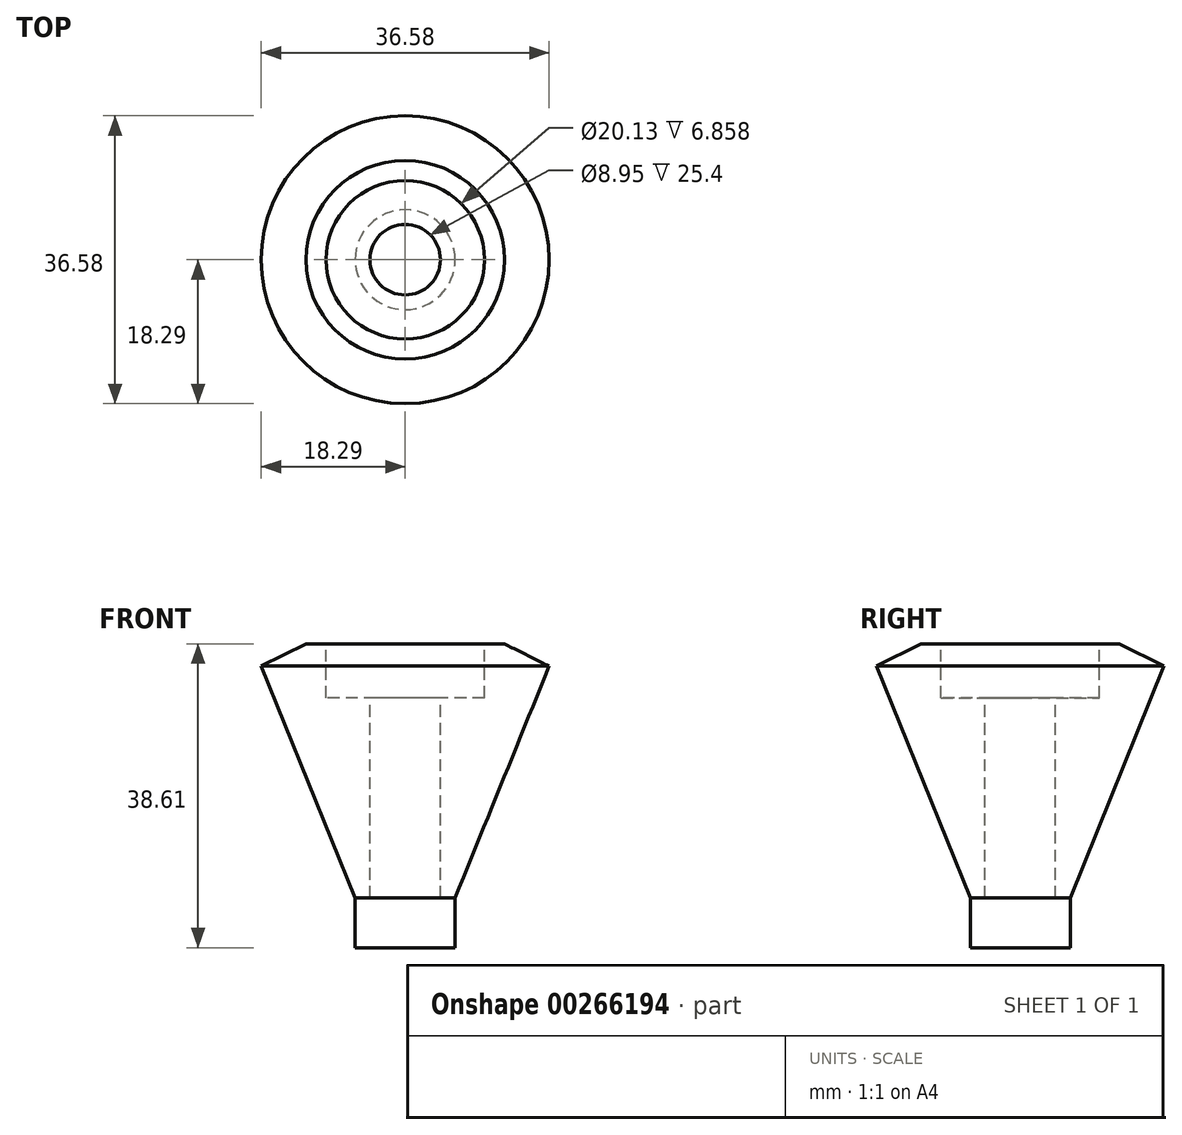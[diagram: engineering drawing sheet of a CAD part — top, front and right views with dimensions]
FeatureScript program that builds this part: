
annotation { "Feature Type Name" : "Feature", "Feature Type Description" : "" }
export const myFeature = defineFeature(function(context is Context, id is Id, definition is map)
    precondition{}
    {
        {
            var Q0;
            Q0=qCreatedBy(makeId("Front.planeOp"),FACE);
            var sketch = newSketch(context, id + "F0", { "sketchPlane" : qUnion([Q0])});
            skLineSegment(sketch, "E0", {"start": v(0, 0) * mm, "end": v(6.35, 0) * mm});
            skLineSegment(sketch, "E1", {"start": v(6.35, 0) * mm, "end": v(6.35, 6.35) * mm});
            skLineSegment(sketch, "E2", {"start": v(6.35, 6.35) * mm, "end": v(18.29, 35.77) * mm});
            skLineSegment(sketch, "E3", {"start": v(18.29, 35.77) * mm, "end": v(12.6, 38.6) * mm});
            skLineSegment(sketch, "E4", {"start": v(12.6, 38.6) * mm, "end": v(10.07, 38.6) * mm});
            skLineSegment(sketch, "E5", {"start": v(10.07, 38.6) * mm, "end": v(10.07, 31.75) * mm});
            skLineSegment(sketch, "E6", {"start": v(10.07, 31.75) * mm, "end": v(4.48, 31.75) * mm});
            skLineSegment(sketch, "E7", {"start": v(4.48, 31.75) * mm, "end": v(4.48, 6.35) * mm});
            skLineSegment(sketch, "E8", {"start": v(4.48, 6.35) * mm, "end": v(0, 6.35) * mm});
            skLineSegment(sketch, "E9", {"start": v(0, 6.35) * mm, "end": v(0, 0) * mm});
            skSolve(sketch);
        }
        {
            var Q0;
            Q0=makeQuery(id+"F0.imprint","IMPRINT",FACE,{"disambiguationData":[TD([[makeQuery(id+"F0.imprint","IMPRINT",EDGE,{"derivedFrom":sQuery(id+"F0.wireOp",EDGE,"E0")}),1.0]])]});
            var Q1;
            Q1=sQuery(id+"F0.wireOp",EDGE,"E9");
            revolve(context, id + "F1", {"entities" : qUnion([Q0]), "axis" : qUnion([Q1]), "revolveType" : RevolveType.FULL});
        }
    });
